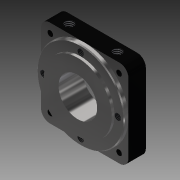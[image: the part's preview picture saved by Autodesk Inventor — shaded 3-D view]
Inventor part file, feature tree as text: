
AUTODESK INVENTOR PART (.ipt)
format: ipt  version: 2013 (Build 170138000, 138)  size: 208,896 bytes
history: native  units: in
note: dims shown in document units (in); Inventor stores cm internally (conversion verified against a paired STEP export)
features: thread x8, extrude x6, sketch x5, fillet x1, chamfer x1
ambient origin geometry x8: Origin, YZ Plane, XZ Plane, XY Plane, X Axis, Y Axis, Z Axis, Center Point
bodies: Solid1 (feature_tree)
feature tree (21):
  sketch  "Sketch1"  dims[d2=1.1024in d7=2.5in]
  extrude  "Extrusion1"  Depth=2.5in
  extrude  "Extrusion2"  Depth=1.063in
  fillet  "Fillet1"  Radius=0.185in
  extrude  "Extrusion3"  Depth=1.063in
  extrude  "Extrusion4"  Depth=2.126in
  thread  "Thread1"  [1 undecoded]
  thread  "Thread2"  [1 undecoded]
  thread  "Thread3"  [1 undecoded]
  thread  "Thread4"  [1 undecoded]
  chamfer  "Chamfer1"  Distance=2.5in
  extrude  "Extrusion5"  Depth=0.1181in TaperAngle=0.0deg
  extrude  "Extrusion6"  Depth=0.0787in TaperAngle=0.0deg
  thread  "Thread5"  [1 undecoded]
  thread  "Thread6"  [1 undecoded]
  thread  "Thread7"  [1 undecoded]
  thread  "Thread8"  [1 undecoded]
  sketch  "Sketch2"  dims[d8=2.5in d9=1.063in d10=0.185in]
  sketch  "Sketch3"  dims[d11=1.063in d12=1.063in]
  sketch  "Sketch4"  dims[d13=1.063in d14=2.126in d15=0.5in d16=0.0in d17=0.1575in d18=0.2756in d19=0.1575in d20=0.0in]
  sketch  "Sketch5"  dims[d21=0.25in d22=2.5in d23=0.1181in d24=0.0in d25=0.0787in d26=0.0in d27=1.0in d28=0.0in d29=1.0in d30=0.0in d31=1.0in d32=0.0in d33=1.0in d34=0.0in d35=0.025in d36=0.125in d37=45.0deg d38=1.378in d40=0.25in d41=0.5in d42=0.0in d43=1.378in d45=0.25in d46=0.5in d47=0.0in d48=1.0in d49=0.0in d50=1.0in d51=0.0in d52=1.0in d53=0.0in d54=1.0in d55=0.0in]
note: 8 required parameter values undecoded (feature->parameter linkage not recoverable at this tier; creation-order binding heuristic only, values carry confidence <= 0.55)
